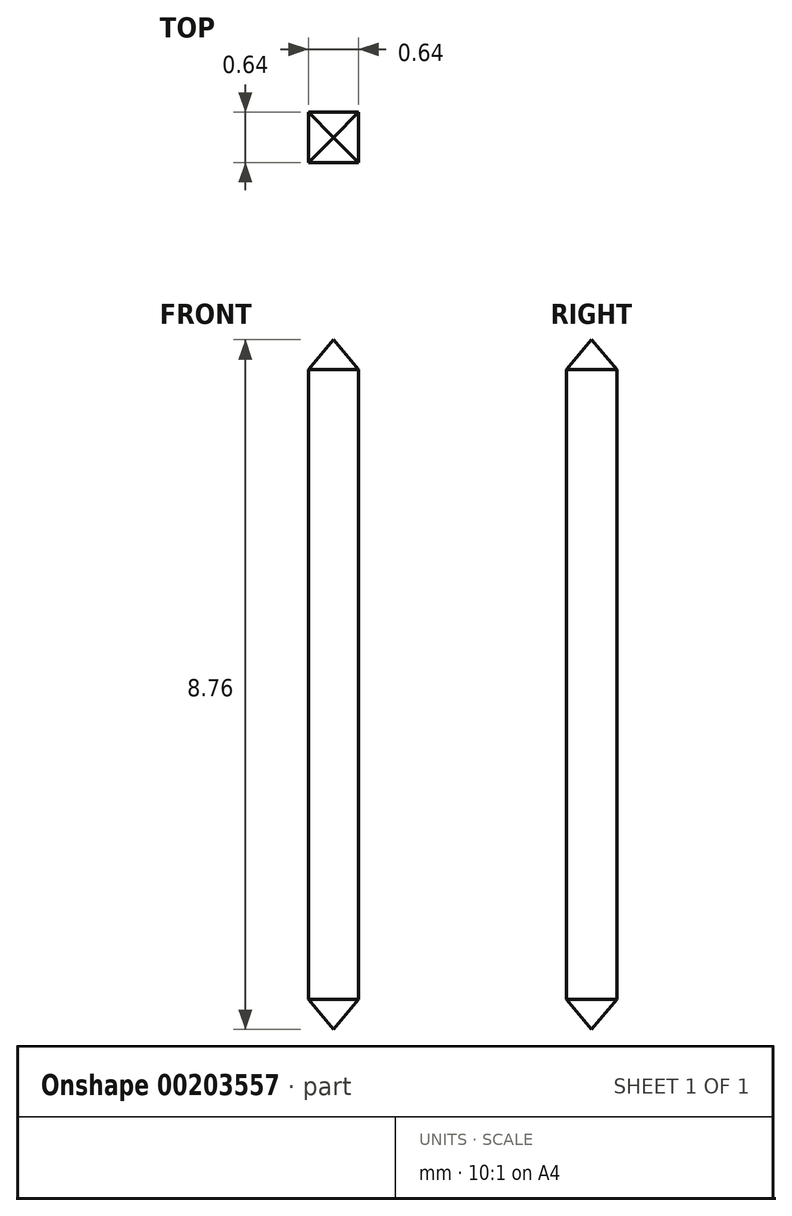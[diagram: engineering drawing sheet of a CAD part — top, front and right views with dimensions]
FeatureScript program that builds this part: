
annotation { "Feature Type Name" : "Feature", "Feature Type Description" : "" }
export const myFeature = defineFeature(function(context is Context, id is Id, definition is map)
    precondition{}
    {
        {
            var Q0;
            Q0=qCreatedBy(makeId("Top.planeOp"),FACE);
            var sketch = newSketch(context, id + "F0", { "sketchPlane" : qUnion([Q0])});
            skLineSegment(sketch, "E0.bottom", {"start": v(0.32, -0.32) * mm, "end": v(-0.32, -0.32) * mm});
            skLineSegment(sketch, "E0.top", {"start": v(0.32, 0.32) * mm, "end": v(-0.32, 0.32) * mm});
            skLineSegment(sketch, "E0.left", {"start": v(0.32, -0.32) * mm, "end": v(0.32, 0.32) * mm});
            skLineSegment(sketch, "E0.right", {"start": v(-0.32, -0.32) * mm, "end": v(-0.32, 0.32) * mm});
            skPoint(sketch, "E0.middle", {"position": v(0, 0) * mm});
            skSolve(sketch);
        }
        {
            var Q0;
            Q0 = qSketchRegion(id + "F0", true);
            extrude(context, id + "F1", {"entities" : qUnion([Q0]), "depth" : 5 * mm});
        }
        {
            var Q0;
            Q0=makeQuery(id+"F1.opExtrude","CAP_FACE",FACE,{"disambiguationData":[OSD([sQuery(id+"F0.wireOp",EDGE,"E0.bottom"),sQuery(id+"F0.wireOp",EDGE,"E0.top"),sQuery(id+"F0.wireOp",EDGE,"E0.left"),sQuery(id+"F0.wireOp",EDGE,"E0.right")])],"isStart":false});
            extrude(context, id + "F2", {"entities" : qUnion([Q0]), "operationType" : NewBodyOperationType.ADD, "depth" : 0.4 * mm, "hasDraft" : true, "draftAngle" : 40 * degree, "draftPullDirection" : true});
        }
        {
            var Q0;
            Q0=makeQuery(id+"F1.opExtrude","CAP_FACE",FACE,{"disambiguationData":[OSD([sQuery(id+"F0.wireOp",EDGE,"E0.bottom"),sQuery(id+"F0.wireOp",EDGE,"E0.top"),sQuery(id+"F0.wireOp",EDGE,"E0.left"),sQuery(id+"F0.wireOp",EDGE,"E0.right")])],"isStart":true});
            extrude(context, id + "F3", {"entities" : qUnion([Q0]), "operationType" : NewBodyOperationType.ADD, "depth" : 3 * mm});
        }
        {
            var Q0;
            Q0=makeQuery(id+"F3.opExtrude","CAP_FACE",FACE,{"disambiguationData":[OSD([sQuery(id+"F0.wireOp",EDGE,"E0.bottom"),sQuery(id+"F0.wireOp",EDGE,"E0.top"),sQuery(id+"F0.wireOp",EDGE,"E0.left"),sQuery(id+"F0.wireOp",EDGE,"E0.right")])],"isStart":false});
            extrude(context, id + "F4", {"entities" : qUnion([Q0]), "operationType" : NewBodyOperationType.ADD, "depth" : 0.4 * mm, "hasDraft" : true, "draftAngle" : 40 * degree, "draftPullDirection" : true});
        }
    });
